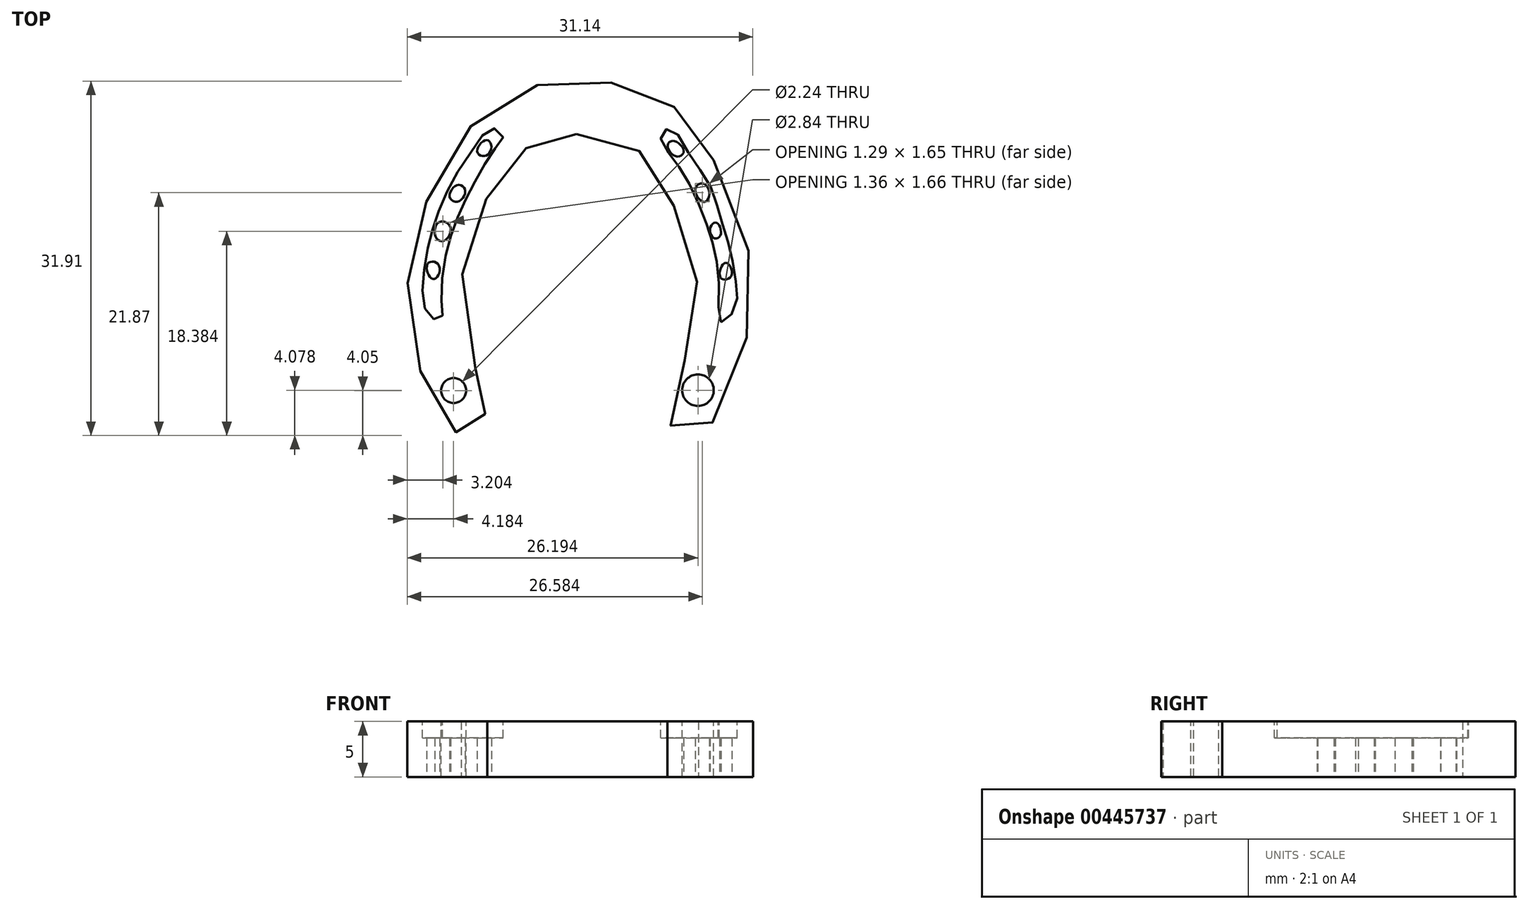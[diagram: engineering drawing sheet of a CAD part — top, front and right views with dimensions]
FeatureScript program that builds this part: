
annotation { "Feature Type Name" : "Feature", "Feature Type Description" : "" }
export const myFeature = defineFeature(function(context is Context, id is Id, definition is map)
    precondition{}
    {
        {
            var Q0;
            Q0=qCreatedBy(makeId("Top.planeOp"),FACE);
            var sketch = newSketch(context, id + "F0", { "sketchPlane" : qUnion([Q0])});
            skLineSegment(sketch, "E0.bottom", {"start": v(17.5, -17.5) * mm, "end": v(-17.5, -17.5) * mm, "construction": true});
            skLineSegment(sketch, "E0.top", {"start": v(17.5, 17.5) * mm, "end": v(-17.5, 17.5) * mm, "construction": true});
            skLineSegment(sketch, "E0.left", {"start": v(17.5, -17.5) * mm, "end": v(17.5, 17.5) * mm, "construction": true});
            skLineSegment(sketch, "E0.right", {"start": v(-17.5, -17.5) * mm, "end": v(-17.5, 17.5) * mm, "construction": true});
            skPoint(sketch, "E0.middle", {"position": v(0, 0) * mm});
            skFitSpline(sketch, "E1", {"points": [v(0, 10.98) * mm, v(3.71, 10.55) * mm, v(6.21, 8.96) * mm, v(7.75, 6.56) * mm, v(9.81, 2.14) * mm, v(10.92, -2.7) * mm, v(10.44, -7.84) * mm, v(8.47, -12.21) * mm, v(8.47, -15.24) * mm, v(9.72, -16.05) * mm, v(11.35, -15.91) * mm, v(13.94, -11.73) * mm, v(15.77, -5.06) * mm, v(15.43, 0.8) * mm, v(12.7, 7.95) * mm, v(10.39, 11.84) * mm, v(8.42, 13.72) * mm, v(5.1, 15.25) * mm, v(1.17, 15.73) * mm, v(-3.25, 15.45) * mm, v(-7.57, 13.57) * mm, v(-11.27, 9.25) * mm, v(-13.9, 3.83) * mm, v(-15.1, -1.46) * mm, v(-14.82, -7.99) * mm, v(-12.8, -12.98) * mm, v(-10.93, -15.81) * mm, v(-9.68, -15.96) * mm, v(-8.67, -15.48) * mm, v(-8.2, -13.99) * mm, v(-8.1, -11.88) * mm, v(-8.63, -11.1) * mm, v(-10.26, -5.15) * mm, v(-9.83, 0.8) * mm, v(-8, 5.31) * mm, v(-5.46, 8.87) * mm, v(-4.35, 9.83) * mm, v(-2.53, 10.7) * mm, v(0, 10.98) * mm]});
            skSolve(sketch);
        }
        {
            var Q0;
            Q0=makeQuery(id+"F0.imprint","IMPRINT",FACE,{"disambiguationData":[TD([[makeQuery(id+"F0.imprint","IMPRINT",EDGE,{"derivedFrom":sQuery(id+"F0.wireOp",EDGE,"E1")}),1.0]])]});
            extrude(context, id + "F1", {"entities" : qUnion([Q0]), "depth" : 5 * mm});
        }
        {
            var Q0;
            Q0=makeQuery(id+"F1.opExtrude","CAP_FACE",FACE,{"disambiguationData":[OSD([sQuery(id+"F0.wireOp",EDGE,"E1")])],"isStart":false});
            var sketch = newSketch(context, id + "F2", { "sketchPlane" : qUnion([Q0])});
            skCircle(sketch, "E2", {"center": v(-11.06, -12.11) * mm, "radius": 1.12 * mm});
            skCircle(sketch, "E3", {"center": v(10.95, -12.08) * mm, "radius": 1.42 * mm});
            skFitSpline(sketch, "E4", {"points": [v(-12.85, -5.68) * mm, v(-13.7, -4.53) * mm, v(-13.77, -1.88) * mm, v(-13.22, 1.45) * mm, v(-12.44, 3.9) * mm, v(-11.02, 7.05) * mm, v(-9.01, 10.04) * mm, v(-7.59, 11.53) * mm, v(-6.6, 10.82) * mm, v(-7.25, 9.8) * mm, v(-8.64, 7.6) * mm, v(-10, 5.01) * mm, v(-11.09, 2.47) * mm, v(-11.87, -0.45) * mm, v(-12.14, -4.19) * mm, v(-12.14, -5.51) * mm, v(-12.85, -5.68) * mm]});
            skFitSpline(sketch, "E5", {"points": [v(13.02, -5.95) * mm, v(14.24, -4.8) * mm, v(14.41, -2.66) * mm, v(13.84, 0.6) * mm, v(12.99, 3.42) * mm, v(12.04, 6.37) * mm, v(10.1, 9.3) * mm, v(8.54, 11.43) * mm, v(7.62, 10.99) * mm, v(8.23, 9.4) * mm, v(9.8, 7.19) * mm, v(11.46, 3.62) * mm, v(12.41, 0.6) * mm, v(12.85, -3.1) * mm, v(13.02, -5.95) * mm]});
            skFitSpline(sketch, "E6", {"points": [v(-8.94, 9.45) * mm, v(-8.23, 9.02) * mm, v(-7.66, 9.9) * mm, v(-8.14, 10.45) * mm, v(-8.94, 9.45) * mm]});
            skFitSpline(sketch, "E7", {"points": [v(-10.77, 6.4) * mm, v(-10.03, 5.96) * mm, v(-10.6, 4.94) * mm, v(-11.4, 5.28) * mm, v(-10.77, 6.4) * mm]});
            skFitSpline(sketch, "E8", {"points": [v(-12.37, 3.05) * mm, v(-11.37, 2.65) * mm, v(-11.88, 1.4) * mm, v(-12.68, 1.74) * mm, v(-12.37, 3.05) * mm]});
            skFitSpline(sketch, "E9", {"points": [v(-13.3, -0.6) * mm, v(-12.4, -0.8) * mm, v(-12.65, -2) * mm, v(-13.28, -1.75) * mm, v(-13.3, -0.6) * mm]});
            skFitSpline(sketch, "E10", {"points": [v(8.85, 10.36) * mm, v(9.67, 9.4) * mm, v(8.96, 8.99) * mm, v(8.23, 9.99) * mm, v(8.85, 10.36) * mm]});
            skFitSpline(sketch, "E11", {"points": [v(11.39, 6.53) * mm, v(11.99, 5.56) * mm, v(11.47, 4.88) * mm, v(10.7, 6.02) * mm, v(11.39, 6.53) * mm]});
            skFitSpline(sketch, "E12", {"points": [v(12.64, 3) * mm, v(12.99, 1.9) * mm, v(12.39, 1.62) * mm, v(12.07, 2.6) * mm, v(12.64, 3) * mm]});
            skFitSpline(sketch, "E13", {"points": [v(13.44, -0.6) * mm, v(13.96, -1.77) * mm, v(12.99, -1.95) * mm, v(13.44, -0.6) * mm]});
            skSolve(sketch);
        }
        {
            var Q0;
            Q0=makeQuery(id+"F2.imprint","IMPRINT",FACE,{"disambiguationData":[TD([[makeQuery(id+"F2.imprint","IMPRINT",EDGE,{"derivedFrom":sQuery(id+"F2.wireOp",EDGE,"E2")}),1.0]])]});
            var Q1;
            Q1=makeQuery(id+"F2.imprint","IMPRINT",FACE,{"disambiguationData":[TD([[makeQuery(id+"F2.imprint","IMPRINT",EDGE,{"derivedFrom":sQuery(id+"F2.wireOp",EDGE,"E3")}),1.0]])]});
            var Q2;
            Q2=makeQuery(id+"F2.imprint","IMPRINT",FACE,{"disambiguationData":[TD([[makeQuery(id+"F2.imprint","IMPRINT",EDGE,{"derivedFrom":sQuery(id+"F2.wireOp",EDGE,"E13")}),-1.0]])]});
            var Q3;
            Q3=makeQuery(id+"F2.imprint","IMPRINT",FACE,{"disambiguationData":[TD([[makeQuery(id+"F2.imprint","IMPRINT",EDGE,{"derivedFrom":sQuery(id+"F2.wireOp",EDGE,"E12")}),-1.0]])]});
            var Q4;
            Q4=makeQuery(id+"F2.imprint","IMPRINT",FACE,{"disambiguationData":[TD([[makeQuery(id+"F2.imprint","IMPRINT",EDGE,{"derivedFrom":sQuery(id+"F2.wireOp",EDGE,"E11")}),-1.0]])]});
            var Q5;
            Q5=makeQuery(id+"F2.imprint","IMPRINT",FACE,{"disambiguationData":[TD([[makeQuery(id+"F2.imprint","IMPRINT",EDGE,{"derivedFrom":sQuery(id+"F2.wireOp",EDGE,"E10")}),-1.0]])]});
            var Q6;
            Q6=makeQuery(id+"F2.imprint","IMPRINT",FACE,{"disambiguationData":[TD([[makeQuery(id+"F2.imprint","IMPRINT",EDGE,{"derivedFrom":sQuery(id+"F2.wireOp",EDGE,"E6")}),1.0]])]});
            var Q7;
            Q7=makeQuery(id+"F2.imprint","IMPRINT",FACE,{"disambiguationData":[TD([[makeQuery(id+"F2.imprint","IMPRINT",EDGE,{"derivedFrom":sQuery(id+"F2.wireOp",EDGE,"E7")}),-1.0]])]});
            var Q8;
            Q8=makeQuery(id+"F2.imprint","IMPRINT",FACE,{"disambiguationData":[TD([[makeQuery(id+"F2.imprint","IMPRINT",EDGE,{"derivedFrom":sQuery(id+"F2.wireOp",EDGE,"E8")}),-1.0]])]});
            var Q9;
            Q9=makeQuery(id+"F2.imprint","IMPRINT",FACE,{"disambiguationData":[TD([[makeQuery(id+"F2.imprint","IMPRINT",EDGE,{"derivedFrom":sQuery(id+"F2.wireOp",EDGE,"E9")}),-1.0]])]});
            extrude(context, id + "F3", {"entities" : qUnion([Q0, Q1, Q2, Q3, Q4, Q5, Q6, Q7, Q8, Q9]), "operationType" : NewBodyOperationType.REMOVE, "oppositeDirection" : true, "depth" : 5 * mm});
        }
        {
            var Q0;
            Q0=makeQuery(id+"F2.imprint","IMPRINT",FACE,{"disambiguationData":[TD([[makeQuery(id+"F2.imprint","IMPRINT",EDGE,{"derivedFrom":sQuery(id+"F2.wireOp",EDGE,"E4")}),-1.0]])]});
            var Q1;
            Q1=makeQuery(id+"F2.imprint","IMPRINT",FACE,{"disambiguationData":[TD([[makeQuery(id+"F2.imprint","IMPRINT",EDGE,{"derivedFrom":sQuery(id+"F2.wireOp",EDGE,"E5")}),1.0]])]});
            extrude(context, id + "F4", {"entities" : qUnion([Q0, Q1]), "operationType" : NewBodyOperationType.REMOVE, "oppositeDirection" : true, "depth" : 1.5 * mm});
        }
    });
